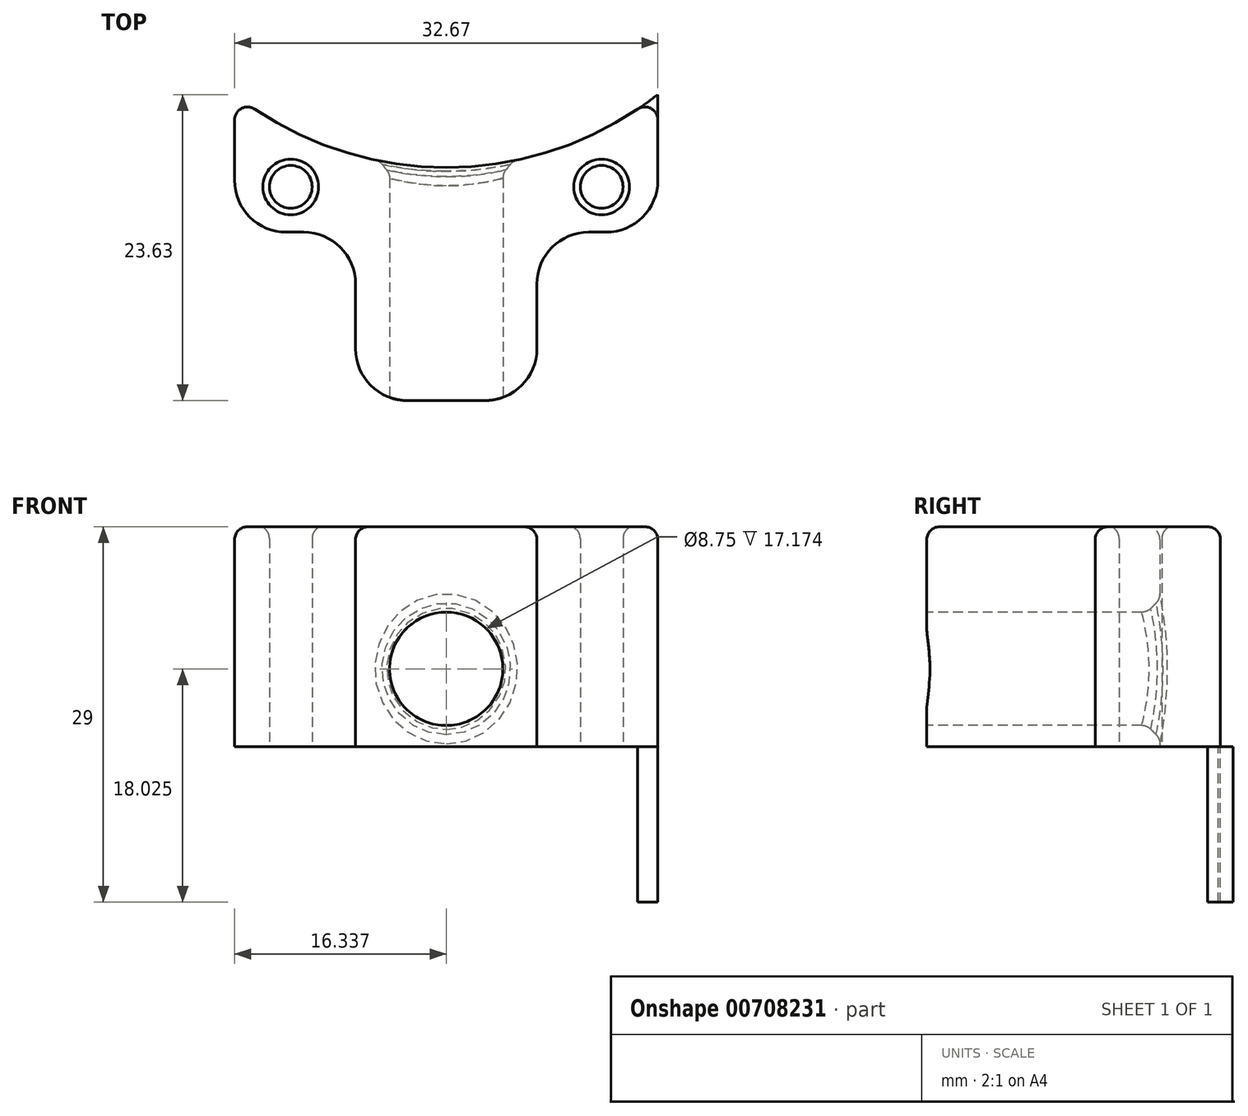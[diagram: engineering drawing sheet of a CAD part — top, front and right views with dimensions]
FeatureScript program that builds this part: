
annotation { "Feature Type Name" : "Feature", "Feature Type Description" : "" }
export const myFeature = defineFeature(function(context is Context, id is Id, definition is map)
    precondition{}
    {
        {
            var Q0;
            Q0=qCreatedBy(makeId("Top.planeOp"),FACE);
            var sketch = newSketch(context, id + "F0", { "sketchPlane" : qUnion([Q0])});
            skLineSegment(sketch, "E0.bottom", {"start": v(0, 0) * mm, "end": v(32.67, 0) * mm});
            skLineSegment(sketch, "E0.top", {"start": v(0, 37.12) * mm, "end": v(32.67, 37.12) * mm});
            skLineSegment(sketch, "E0.left", {"start": v(0, 0) * mm, "end": v(0, 37.12) * mm});
            skLineSegment(sketch, "E0.right", {"start": v(32.67, 0) * mm, "end": v(32.67, 37.12) * mm});
            skLineSegment(sketch, "E1", {"start": v(0, 16.5) * mm, "end": v(32.67, 16.5) * mm, "construction": true});
            skPoint(sketch, "E2", {"position": v(4.34, 16.5) * mm});
            skPoint(sketch, "E3", {"position": v(28.34, 16.5) * mm});
            skLineSegment(sketch, "E4", {"start": v(16.34, 37.12) * mm, "end": v(16.34, 0) * mm, "construction": true});
            skCircle(sketch, "E5", {"center": v(4.34, 16.5) * mm, "radius": 1.65 * mm});
            skLineSegment(sketch, "E6", {"start": v(16.34, 37.12) * mm, "end": v(16.34, 104.14) * mm, "construction": true});
            skCircle(sketch, "E7", {"center": v(16.34, 44.5) * mm, "radius": 26.5 * mm});
            skCircle(sketch, "E8.MirrorC", {"center": v(28.34, 16.5) * mm, "radius": 1.65 * mm});
            skLineSegment(sketch, "E9", {"start": v(0, 13) * mm, "end": v(9.34, 13) * mm});
            skLineSegment(sketch, "E10", {"start": v(9.34, 13) * mm, "end": v(9.34, 0) * mm});
            skLineSegment(sketch, "E11.MirrorCS", {"start": v(23.34, 13) * mm, "end": v(23.34, 0) * mm});
            skLineSegment(sketch, "E12.MirrorCS", {"start": v(32.67, 13) * mm, "end": v(23.34, 13) * mm});
            skSolve(sketch);
        }
        {
            var Q0;
            Q0=makeQuery(id+"F0.imprint","IMPRINT",FACE,{"disambiguationData":[TD([[makeQuery(id+"F0.imprint","IMPRINT",EDGE,{"derivedFrom":sQuery(id+"F0.wireOp",EDGE,"E5")}),-1.0]])]});
            extrude(context, id + "F1", {"entities" : qUnion([Q0]), "depth" : 17 * mm, "offsetDistance" : 25 * mm});
        }
        {
            var Q0;
            Q0=makeQuery(id+"F1.opExtrude","SWEPT_FACE",FACE,{"disambiguationData":[OSD([sQuery(id+"F0.wireOp",EDGE,"E0.bottom")])]});
            var sketch = newSketch(context, id + "F2", { "sketchPlane" : qUnion([Q0])});
            skLineSegment(sketch, "E13", {"start": v(16.34, 17) * mm, "end": v(16.34, 0) * mm, "construction": true});
            skCircle(sketch, "E14", {"center": v(16.34, 6.03) * mm, "radius": 4.38 * mm});
            skSolve(sketch);
        }
        {
            var Q0;
            Q0=makeQuery(id+"F2.imprint","IMPRINT",FACE,{"disambiguationData":[TD([[makeQuery(id+"F2.imprint","IMPRINT",EDGE,{"derivedFrom":sQuery(id+"F2.wireOp",EDGE,"E14")}),1.0]])]});
            extrude(context, id + "F3", {"entities" : qUnion([Q0]), "operationType" : NewBodyOperationType.REMOVE, "endBound" : BoundingType.THROUGH_ALL, "oppositeDirection" : true, "depth" : 25 * mm, "offsetDistance" : 25 * mm});
        }
        {
            var Q0;
            Q0=makeQuery(id+"F1.opExtrude","SWEPT_EDGE",EDGE,{"disambiguationData":[OSD([sQuery(id+"F0.wireOp",EDGE,"E0.left"),sQuery(id+"F0.wireOp",EDGE,"E9")])]});
            var Q1;
            Q1=makeQuery(id+"F1.opExtrude","SWEPT_EDGE",EDGE,{"disambiguationData":[OSD([sQuery(id+"F0.wireOp",EDGE,"E0.right"),sQuery(id+"F0.wireOp",EDGE,"E12.MirrorCS")])]});
            var Q2;
            Q2=makeQuery(id+"F1.opExtrude","SWEPT_EDGE",EDGE,{"disambiguationData":[OSD([sQuery(id+"F0.wireOp",EDGE,"E11.MirrorCS"),sQuery(id+"F0.wireOp",EDGE,"E12.MirrorCS")])]});
            var Q3;
            Q3=makeQuery(id+"F1.opExtrude","SWEPT_EDGE",EDGE,{"disambiguationData":[OSD([sQuery(id+"F0.wireOp",EDGE,"E9"),sQuery(id+"F0.wireOp",EDGE,"E10")])]});
            var Q4;
            Q4=makeQuery(id+"F1.opExtrude","SWEPT_EDGE",EDGE,{"disambiguationData":[OSD([sQuery(id+"F0.wireOp",EDGE,"E0.bottom"),sQuery(id+"F0.wireOp",EDGE,"E10")])]});
            var Q5;
            Q5=makeQuery(id+"F1.opExtrude","SWEPT_EDGE",EDGE,{"disambiguationData":[OSD([sQuery(id+"F0.wireOp",EDGE,"E0.bottom"),sQuery(id+"F0.wireOp",EDGE,"E11.MirrorCS")])]});
            fillet(context, id + "F4", {"entities" : qUnion([Q0, Q1, Q2, Q3, Q4, Q5]), "radius" : 4 * mm, "tangentPropagation" : true, "allowEdgeOverflow" : false});
        }
        {
            var Q0;
            Q0=makeQuery(id+"F3.boolean.opBoolean","INTERSECT",EDGE,{"derivedFrom":[makeQuery(id+"F1.opExtrude","SWEPT_FACE",FACE,{"disambiguationData":[OSD([sQuery(id+"F0.wireOp",EDGE,"E7")])]}),makeQuery(id+"F3.opExtrude","SWEPT_FACE",FACE,{"disambiguationData":[OSD([sQuery(id+"F2.wireOp",EDGE,"E14")])]})]});
            chamfer(context, id + "F5", {"entities" : qUnion([Q0]), "width" : 1 * mm, "tangentPropagation" : true});
        }
        {
            var Q0;
            Q0=makeQuery(id+"F1.opExtrude","CAP_EDGE",EDGE,{"disambiguationData":[OSD([sQuery(id+"F0.wireOp",EDGE,"E5")])],"isStart":false});
            var Q1;
            Q1=makeQuery(id+"F1.opExtrude","CAP_EDGE",EDGE,{"disambiguationData":[OSD([sQuery(id+"F0.wireOp",EDGE,"E8.MirrorC")])],"isStart":false});
            chamfer(context, id + "F6", {"entities" : qUnion([Q0, Q1]), "width" : 0.5 * mm, "tangentPropagation" : true});
        }
        {
            var Q0;
            Q0=makeQuery(id+"F1.opExtrude","SWEPT_EDGE",EDGE,{"disambiguationData":[OSD([sQuery(id+"F0.wireOp",EDGE,"E0.left"),sQuery(id+"F0.wireOp",EDGE,"E7")])]});
            var Q1;
            Q1=makeQuery(id+"F1.opExtrude","SWEPT_EDGE",EDGE,{"disambiguationData":[OSD([sQuery(id+"F0.wireOp",EDGE,"E0.right"),sQuery(id+"F0.wireOp",EDGE,"E7")])]});
            var Q2;
            Q2=makeQuery(id+"F1.opExtrude","CAP_EDGE",EDGE,{"disambiguationData":[OSD([sQuery(id+"F0.wireOp",EDGE,"E7")])],"isStart":false});
            var Q3;
            {var subQ0=sQuery(id+"F0.wireOp",EDGE,"E10");var subQ1=sQuery(id+"F0.wireOp",EDGE,"E9");Q3=makeQuery(id+"F4.opFillet","BLEND_EDGE",EDGE,{"blendedFrom":[makeQuery(id+"F1.opExtrude","SWEPT_EDGE",EDGE,{"disambiguationData":[OSD([subQ1,subQ0])]}),makeQuery(id+"F1.opExtrude","CAP_FACE",FACE,{"disambiguationData":[OSD([sQuery(id+"F0.wireOp",EDGE,"E0.bottom"),sQuery(id+"F0.wireOp",EDGE,"E0.left"),sQuery(id+"F0.wireOp",EDGE,"E0.right"),sQuery(id+"F0.wireOp",EDGE,"E5"),sQuery(id+"F0.wireOp",EDGE,"E7"),sQuery(id+"F0.wireOp",EDGE,"E8.MirrorC"),subQ1,subQ0,sQuery(id+"F0.wireOp",EDGE,"E11.MirrorCS"),sQuery(id+"F0.wireOp",EDGE,"E12.MirrorCS")])],"isStart":false})],"blendedInto":[makeQuery(id+"F1.opExtrude","CAP_FACE",FACE,{"disambiguationData":[OSD([sQuery(id+"F0.wireOp",EDGE,"E0.bottom"),sQuery(id+"F0.wireOp",EDGE,"E0.left"),sQuery(id+"F0.wireOp",EDGE,"E0.right"),sQuery(id+"F0.wireOp",EDGE,"E5"),sQuery(id+"F0.wireOp",EDGE,"E7"),sQuery(id+"F0.wireOp",EDGE,"E8.MirrorC"),subQ1,subQ0,sQuery(id+"F0.wireOp",EDGE,"E11.MirrorCS"),sQuery(id+"F0.wireOp",EDGE,"E12.MirrorCS")])],"isStart":false})]});}
            var Q4;
            Q4=makeQuery(id+"F3.boolean.opBoolean","COPY",EDGE,{"derivedFrom":makeQuery(id+"F3.opExtrude","CAP_EDGE",EDGE,{"disambiguationData":[OSD([sQuery(id+"F2.wireOp",EDGE,"E14")])],"isStart":true})});
            var Q5;
            {var subQ0=makeQuery(id+"F3.opExtrude","SWEPT_FACE",FACE,{"disambiguationData":[OSD([sQuery(id+"F2.wireOp",EDGE,"E14")])]});Q5=makeQuery(id+"F5.opChamfer","BLEND_EDGE",EDGE,{"blendedFrom":[makeQuery(id+"F3.boolean.opBoolean","INTERSECT",EDGE,{"derivedFrom":[makeQuery(id+"F1.opExtrude","SWEPT_FACE",FACE,{"disambiguationData":[OSD([sQuery(id+"F0.wireOp",EDGE,"E7")])]}),subQ0]}),makeQuery(id+"F3.boolean.opBoolean","COPY",FACE,{"derivedFrom":subQ0})],"blendedInto":[makeQuery(id+"F3.boolean.opBoolean","COPY",FACE,{"derivedFrom":subQ0})]});}
            var Q6;
            {var subQ0=makeQuery(id+"F1.opExtrude","SWEPT_FACE",FACE,{"disambiguationData":[OSD([sQuery(id+"F0.wireOp",EDGE,"E7")])]});Q6=makeQuery(id+"F5.opChamfer","BLEND_EDGE",EDGE,{"blendedFrom":[makeQuery(id+"F3.boolean.opBoolean","INTERSECT",EDGE,{"derivedFrom":[subQ0,makeQuery(id+"F3.opExtrude","SWEPT_FACE",FACE,{"disambiguationData":[OSD([sQuery(id+"F2.wireOp",EDGE,"E14")])]})]}),subQ0],"blendedInto":[subQ0]});}
            var Q7;
            {var subQ0=sQuery(id+"F0.wireOp",EDGE,"E5");Q7=makeQuery(id+"F6.opChamfer","BLEND_EDGE",EDGE,{"blendedFrom":[makeQuery(id+"F1.opExtrude","CAP_EDGE",EDGE,{"disambiguationData":[OSD([subQ0])],"isStart":false}),makeQuery(id+"F1.opExtrude","SWEPT_FACE",FACE,{"disambiguationData":[OSD([subQ0])]})],"blendedInto":[makeQuery(id+"F1.opExtrude","SWEPT_FACE",FACE,{"disambiguationData":[OSD([subQ0])]})]});}
            var Q8;
            {var subQ0=sQuery(id+"F0.wireOp",EDGE,"E8.MirrorC");Q8=makeQuery(id+"F6.opChamfer","BLEND_EDGE",EDGE,{"blendedFrom":[makeQuery(id+"F1.opExtrude","CAP_EDGE",EDGE,{"disambiguationData":[OSD([subQ0])],"isStart":false}),makeQuery(id+"F1.opExtrude","SWEPT_FACE",FACE,{"disambiguationData":[OSD([subQ0])]})],"blendedInto":[makeQuery(id+"F1.opExtrude","SWEPT_FACE",FACE,{"disambiguationData":[OSD([subQ0])]})]});}
            fillet(context, id + "F7", {"entities" : qUnion([Q0, Q1, Q2, Q3, Q4, Q5, Q6, Q7, Q8]), "radius" : 1 * mm, "tangentPropagation" : true, "allowEdgeOverflow" : false});
        }
        {
            var Q0;
            Q0=makeQuery(id+"F0.imprint","IMPRINT",FACE,{"disambiguationData":[TD([[makeQuery(id+"F0.imprint","IMPRINT",EDGE,{"derivedFrom":sQuery(id+"F0.wireOp",EDGE,"E5")}),-1.0]])]});
            var sketch = newSketch(context, id + "F8", { "sketchPlane" : qUnion([Q0])});
            skArc(sketch, "E15.0", {"start": v(31.12, 22.5) * mm, "mid": v(32.14, 22.56) * mm, "end": v(32.67, 21.67) * mm});
            skArc(sketch, "E16.0", {"start": v(1.56, 22.5) * mm, "mid": v(16.34, 18) * mm, "end": v(31.12, 22.5) * mm});
            skLineSegment(sketch, "E17.0", {"start": v(32.67, 17) * mm, "end": v(32.67, 21.67) * mm});
            skArc(sketch, "E18.0", {"start": v(32.67, 17) * mm, "mid": v(31.5, 14.17) * mm, "end": v(28.67, 13) * mm});
            skArc(sketch, "E19.0", {"start": v(4, 13) * mm, "mid": v(1.17, 14.17) * mm, "end": v(0, 17) * mm});
            skLineSegment(sketch, "E20.0", {"start": v(0, 17) * mm, "end": v(0, 21.67) * mm});
            skArc(sketch, "E21.0", {"start": v(0, 21.67) * mm, "mid": v(0.53, 22.56) * mm, "end": v(1.56, 22.5) * mm});
            skLineSegment(sketch, "E22.0", {"start": v(4, 13) * mm, "end": v(9.34, 13) * mm});
            skPoint(sketch, "E23.orphan", {"position": v(32.67, 0) * mm});
            skPoint(sketch, "E24.0.2.start.orphan", {"position": v(23.34, 0) * mm});
            skPoint(sketch, "E25.orphan", {"position": v(0, 0) * mm});
            skPoint(sketch, "E26.orphan", {"position": v(0, 13) * mm});
            skPoint(sketch, "E27.orphan", {"position": v(0, 37.12) * mm});
            skPoint(sketch, "E28.orphan", {"position": v(32.67, 37.12) * mm});
            skPoint(sketch, "E29.orphan", {"position": v(32.67, 13) * mm});
            skPoint(sketch, "E24.0.0.end.orphan", {"position": v(23.34, 13) * mm});
            skLineSegment(sketch, "E30", {"start": v(28.67, 13) * mm, "end": v(9.34, 13) * mm});
            skSolve(sketch);
        }
        {
            var Q0;
            Q0=makeQuery(id+"F8.imprint","IMPRINT",FACE,{"disambiguationData":[TD([[makeQuery(id+"F8.imprint","IMPRINT",EDGE,{"derivedFrom":sQuery(id+"F8.wireOp",EDGE,"E15.0")}),-1.0]])]});
            extrude(context, id + "F9", {"entities" : qUnion([Q0]), "operationType" : NewBodyOperationType.ADD, "oppositeDirection" : true, "depth" : 12 * mm, "offsetDistance" : 25 * mm});
        }
    });
